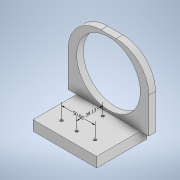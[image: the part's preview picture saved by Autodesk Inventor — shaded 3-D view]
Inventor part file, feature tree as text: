
AUTODESK INVENTOR PART (.ipt)
format: ipt  version: 2022 (Build 260153000, 153)  size: 166,400 bytes
history: native  units: mm
features: extrude x5, sketch x5, other x3, chamfer x1, fillet x1
ambient origin geometry x8: Origin, YZ Plane, XZ Plane, XY Plane, X Axis, Y Axis, Z Axis, Center Point
bodies: Solid1 (feature_tree)
feature tree (15):
  other  "Annotations"
  extrude  "Extrusion1"  Depth=75.0mm
  extrude  "Extrusion2"  Depth=12.7mm
  extrude  "Extrusion4"  Depth=9.906mm
  extrude  "Extrusion5"  Depth=101.6mm
  extrude  "Extrusion6"  TaperAngle=0.0deg  [1 undecoded]
  chamfer  "Chamfer1"  Distance=95.0mm
  fillet  "Fillet1"  [1 undecoded]
  sketch  "Sketch1"  dims[d0=94.996mm d1=75.0mm]
  sketch  "Sketch2"  dims[d2=15.0mm d3=0.0mm d4=12.7mm]
  sketch  "Sketch4"  dims[d5=12.7mm d6=9.906mm]
  sketch  "Sketch5"  dims[d7=101.6mm d8=0.0mm d12=4.0mm]
  sketch  "Sketch6"  dims[d13=4.0mm d14=0.0mm d15=0.0mm d17=95.0mm d18=0.0mm d19=0.0mm d23=4.0mm d24=0.0mm d25=0.0mm d26=2.0mm d27=2.0mm d28=45.0deg d30=48.75mm d16=39.126314mm d29=50.0mm]
  other  "Linear Dimension 1"
  other  "Linear Dimension 2"
note: 2 required parameter values undecoded (feature->parameter linkage not recoverable at this tier; creation-order binding heuristic only, values carry confidence <= 0.55)
